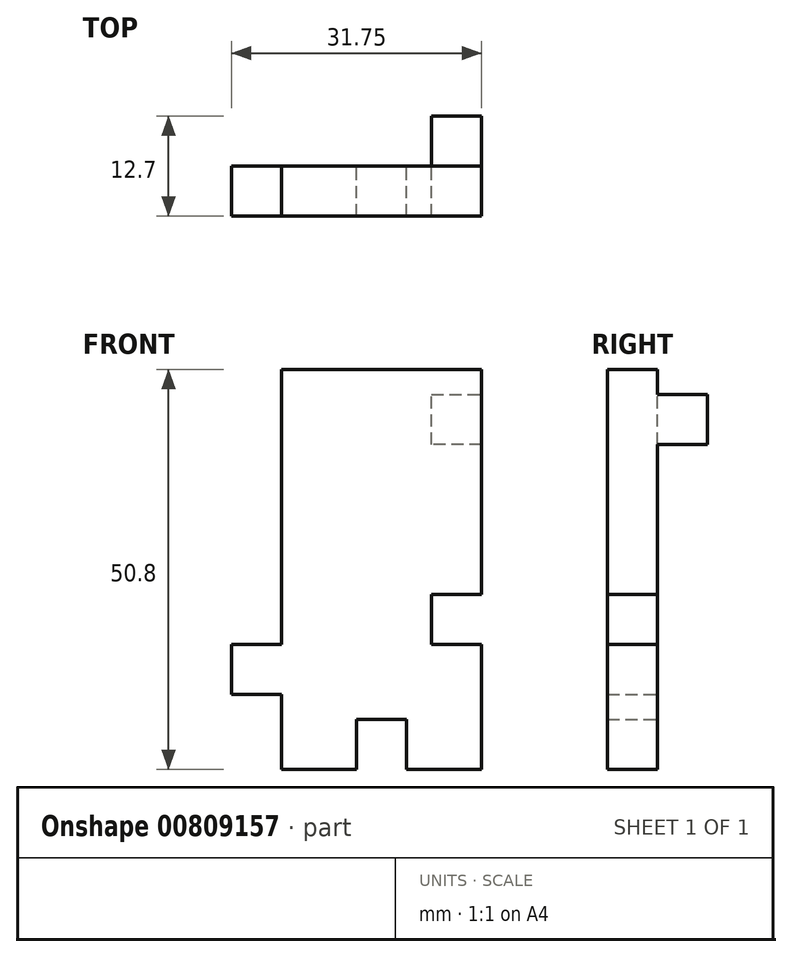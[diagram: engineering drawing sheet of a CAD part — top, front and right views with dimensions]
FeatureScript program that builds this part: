
annotation { "Feature Type Name" : "Feature", "Feature Type Description" : "" }
export const myFeature = defineFeature(function(context is Context, id is Id, definition is map)
    precondition{}
    {
        {
            var Q0;
            Q0=qCreatedBy(makeId("Front.planeOp"),FACE);
            var sketch = newSketch(context, id + "F0", { "sketchPlane" : qUnion([Q0])});
            skLineSegment(sketch, "E0", {"start": v(-1.79, 25.4) * mm, "end": v(-14.49, 25.4) * mm});
            skLineSegment(sketch, "E1", {"start": v(-14.49, 25.4) * mm, "end": v(-14.49, 0) * mm});
            skLineSegment(sketch, "E2.MirrorCS", {"start": v(-1.79, 25.4) * mm, "end": v(10.91, 25.4) * mm});
            skLineSegment(sketch, "E3.MirrorCS", {"start": v(-14.49, -25.4) * mm, "end": v(-14.49, -15.87) * mm});
            skLineSegment(sketch, "E4.MirrorCS", {"start": v(10.91, -25.4) * mm, "end": v(10.91, -15.87) * mm});
            skPoint(sketch, "E5.MirrorCS.end.orphan", {"position": v(12.7, 0) * mm});
            skPoint(sketch, "E5.MirrorCS.start.orphan", {"position": v(0, 0) * mm});
            skLineSegment(sketch, "E6", {"start": v(-14.49, -25.4) * mm, "end": v(-4.96, -25.4) * mm});
            skLineSegment(sketch, "E7", {"start": v(-4.96, -25.4) * mm, "end": v(-4.96, -19.05) * mm});
            skLineSegment(sketch, "E8", {"start": v(-4.96, -19.05) * mm, "end": v(1.39, -19.05) * mm});
            skLineSegment(sketch, "E9", {"start": v(1.39, -25.4) * mm, "end": v(1.39, -19.05) * mm});
            skLineSegment(sketch, "E10.trimOffspring", {"start": v(1.39, -25.4) * mm, "end": v(10.91, -25.4) * mm});
            skPoint(sketch, "E11.orphan", {"position": v(-1.79, -25.4) * mm});
            skLineSegment(sketch, "E12", {"start": v(10.91, -9.52) * mm, "end": v(4.56, -9.52) * mm});
            skLineSegment(sketch, "E13.trimOffspring", {"start": v(10.91, -3.17) * mm, "end": v(10.91, 0) * mm});
            skPoint(sketch, "E14.end.orphan", {"position": v(10.91, -12.7) * mm});
            skLineSegment(sketch, "E15", {"start": v(-14.49, 25.4) * mm, "end": v(-14.49, -9.52) * mm});
            skLineSegment(sketch, "E16", {"start": v(10.91, 25.4) * mm, "end": v(10.91, -3.17) * mm});
            skLineSegment(sketch, "E17", {"start": v(-14.49, -9.52) * mm, "end": v(-20.84, -9.52) * mm});
            skLineSegment(sketch, "E18", {"start": v(-20.84, -9.52) * mm, "end": v(-20.84, -15.87) * mm});
            skLineSegment(sketch, "E19", {"start": v(-14.49, -15.87) * mm, "end": v(-20.84, -15.87) * mm});
            skLineSegment(sketch, "E20.trimOffspring", {"start": v(-14.49, -15.87) * mm, "end": v(-14.49, -25.4) * mm});
            skLineSegment(sketch, "E21.trimOffspring", {"start": v(-14.49, -9.52) * mm, "end": v(-14.49, 0) * mm});
            skPoint(sketch, "E22.start.orphan", {"position": v(-14.49, -12.7) * mm});
            skLineSegment(sketch, "E23", {"start": v(-14.49, 12.7) * mm, "end": v(-14.49, 5.73) * mm});
            skLineSegment(sketch, "E24", {"start": v(-14.49, 5.73) * mm, "end": v(-14.49, 12.7) * mm});
            skLineSegment(sketch, "E25", {"start": v(4.56, -9.52) * mm, "end": v(4.56, -3.17) * mm});
            skLineSegment(sketch, "E26", {"start": v(4.56, -3.17) * mm, "end": v(10.91, -3.17) * mm});
            skLineSegment(sketch, "E27", {"start": v(10.91, -9.52) * mm, "end": v(10.91, -15.87) * mm});
            skPoint(sketch, "E28.end.orphan", {"position": v(4.56, -15.87) * mm});
            skLineSegment(sketch, "E29", {"start": v(10.91, 25.4) * mm, "end": v(10.91, 22.22) * mm});
            skLineSegment(sketch, "E30", {"start": v(10.91, 22.22) * mm, "end": v(10.91, 25.4) * mm});
            skLineSegment(sketch, "E31", {"start": v(10.91, 22.22) * mm, "end": v(4.56, 22.22) * mm});
            skLineSegment(sketch, "E32", {"start": v(4.56, 22.22) * mm, "end": v(4.56, 15.87) * mm});
            skLineSegment(sketch, "E33", {"start": v(4.56, 15.87) * mm, "end": v(10.91, 15.87) * mm});
            skSolve(sketch);
        }
        {
            var Q0;
            Q0 = qSketchRegion(id + "F0", true);
            extrude(context, id + "F1", {"entities" : qUnion([Q0]), "depth" : 6.35 * mm, "offsetDistance" : 25.4 * mm});
        }
        {
            var Q0;
            {var subQ0=sQuery(id+"F0.wireOp",EDGE,"E31");Q0=makeQuery(id+"F0.imprint","IMPRINT",FACE,{"disambiguationData":[TD([[makeQuery(id+"F0.imprint","IMPRINT",EDGE,{"derivedFrom":subQ0}),1.0]])]});}
            extrude(context, id + "F2", {"entities" : qUnion([Q0]), "operationType" : NewBodyOperationType.ADD, "endBound" : BoundingType.SYMMETRIC, "depth" : 12.7 * mm, "offsetDistance" : 25.4 * mm});
        }
    });
